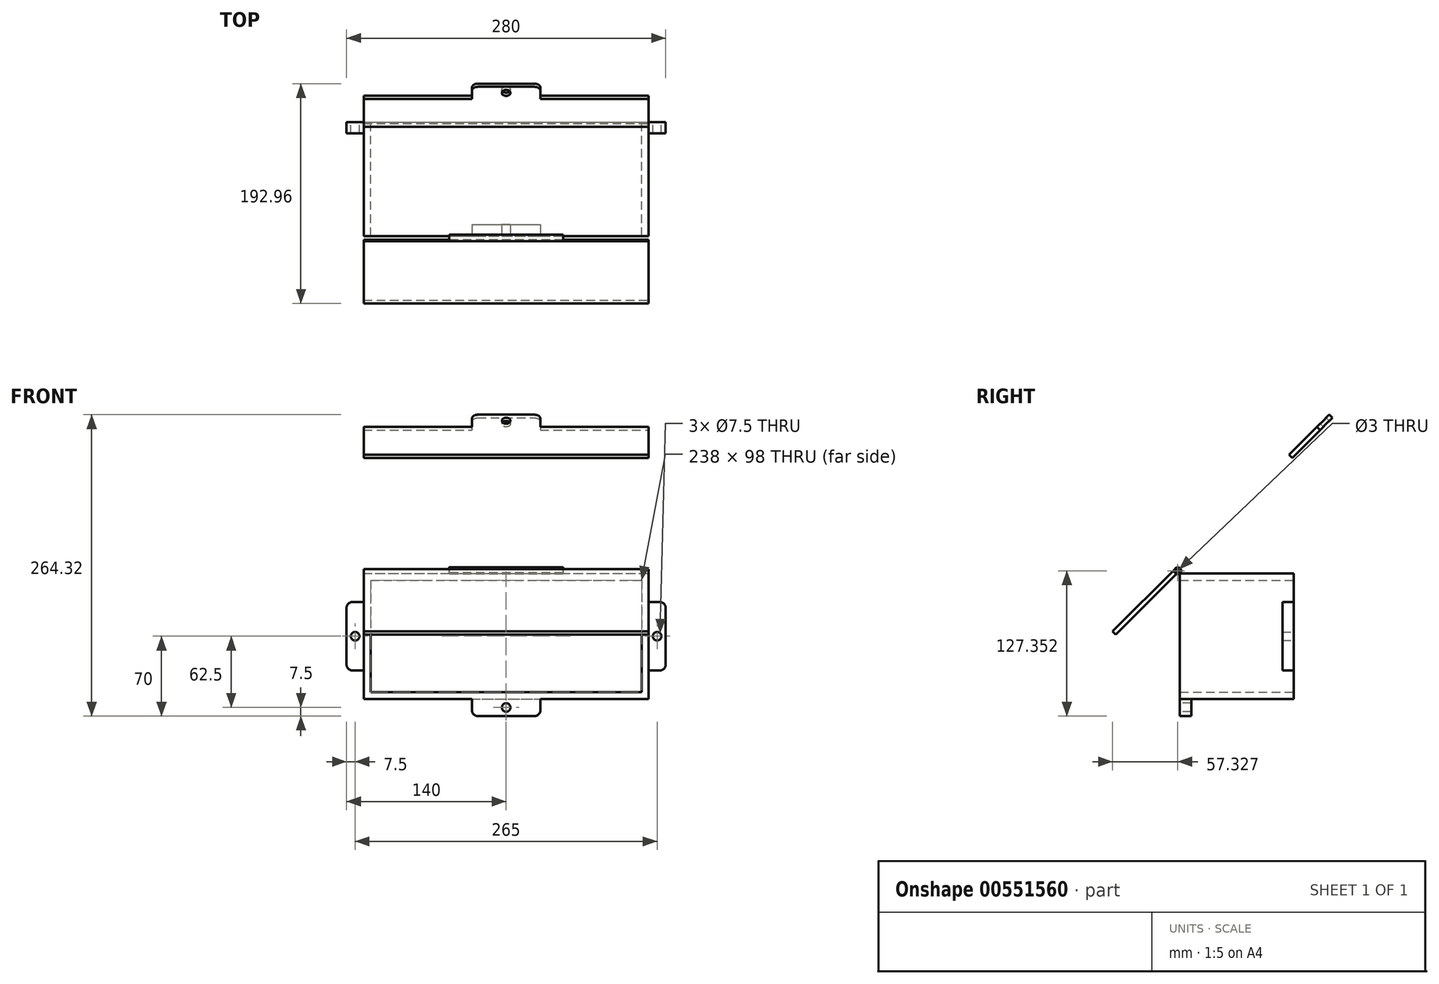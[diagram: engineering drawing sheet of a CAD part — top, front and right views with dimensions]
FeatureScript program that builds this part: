
annotation { "Feature Type Name" : "Feature", "Feature Type Description" : "" }
export const myFeature = defineFeature(function(context is Context, id is Id, definition is map)
    precondition{}
    {
        {
            var Q0;
            Q0=qCreatedBy(makeId("Front.planeOp"),FACE);
            var sketch = newSketch(context, id + "F0", { "sketchPlane" : qUnion([Q0])});
            skLineSegment(sketch, "E0.bottom", {"start": v(-125, 55) * mm, "end": v(125, 55) * mm});
            skLineSegment(sketch, "E0.top", {"start": v(-125, -55) * mm, "end": v(125, -55) * mm});
            skLineSegment(sketch, "E0.left", {"start": v(-125, 55) * mm, "end": v(-125, -55) * mm});
            skLineSegment(sketch, "E0.right", {"start": v(125, 55) * mm, "end": v(125, -55) * mm});
            skLineSegment(sketch, "E1", {"start": v(-125, 30) * mm, "end": v(-140, 30) * mm});
            skLineSegment(sketch, "E2", {"start": v(-140, 30) * mm, "end": v(-140, -30) * mm});
            skLineSegment(sketch, "E3", {"start": v(-140, -30) * mm, "end": v(-125, -30) * mm});
            skCircle(sketch, "E4", {"center": v(-132.5, 0) * mm, "radius": 3.75 * mm});
            skPoint(sketch, "E4.centerSnap0", {"position": v(-125, 0) * mm});
            skLineSegment(sketch, "E5", {"start": v(125, 30) * mm, "end": v(140, 30) * mm});
            skLineSegment(sketch, "E6", {"start": v(140, 30) * mm, "end": v(140, -30) * mm});
            skLineSegment(sketch, "E7", {"start": v(140, -30) * mm, "end": v(125, -30) * mm});
            skCircle(sketch, "E8", {"center": v(132.5, 0) * mm, "radius": 3.75 * mm});
            skLineSegment(sketch, "E9.bottom", {"start": v(-119, 49) * mm, "end": v(119, 49) * mm});
            skLineSegment(sketch, "E9.top", {"start": v(-119, -49) * mm, "end": v(119, -49) * mm});
            skLineSegment(sketch, "E9.left", {"start": v(-119, 49) * mm, "end": v(-119, -49) * mm});
            skLineSegment(sketch, "E9.right", {"start": v(119, 49) * mm, "end": v(119, -49) * mm});
            skSolve(sketch);
        }
        {
            var Q0;
            {var subQ4=sQuery(id+"F0.wireOp",EDGE,"E0.bottom");Q0=makeQuery(id+"F0.imprint","IMPRINT",FACE,{"disambiguationData":[TD([[makeQuery(id+"F0.imprint","IMPRINT",EDGE,{"derivedFrom":subQ4}),-1.0]])]});}
            extrude(context, id + "F1", {"entities" : qUnion([Q0]), "depth" : 100 * mm, "offsetDistance" : 25 * mm});
        }
        {
            var Q0;
            {var subQ1=sQuery(id+"F0.wireOp",EDGE,"E5");Q0=makeQuery(id+"F0.imprint","IMPRINT",FACE,{"disambiguationData":[TD([[makeQuery(id+"F0.imprint","IMPRINT",EDGE,{"derivedFrom":subQ1}),-1.0]])]});}
            var Q1;
            {var subQ1=sQuery(id+"F0.wireOp",EDGE,"E1");Q1=makeQuery(id+"F0.imprint","IMPRINT",FACE,{"disambiguationData":[TD([[makeQuery(id+"F0.imprint","IMPRINT",EDGE,{"derivedFrom":subQ1}),1.0]])]});}
            extrude(context, id + "F2", {"entities" : qUnion([Q0, Q1]), "operationType" : NewBodyOperationType.ADD, "depth" : 10 * mm, "offsetDistance" : 25 * mm});
        }
        {
            var Q0;
            Q0=makeQuery(id+"F2.opExtrude","SWEPT_EDGE",EDGE,{"disambiguationData":[OSD([sQuery(id+"F0.wireOp",EDGE,"E5"),sQuery(id+"F0.wireOp",EDGE,"E6")])]});
            var Q1;
            Q1=makeQuery(id+"F2.opExtrude","SWEPT_EDGE",EDGE,{"disambiguationData":[OSD([sQuery(id+"F0.wireOp",EDGE,"E6"),sQuery(id+"F0.wireOp",EDGE,"E7")])]});
            var Q2;
            Q2=makeQuery(id+"F2.opExtrude","SWEPT_EDGE",EDGE,{"disambiguationData":[OSD([sQuery(id+"F0.wireOp",EDGE,"E2"),sQuery(id+"F0.wireOp",EDGE,"E3")])]});
            var Q3;
            Q3=makeQuery(id+"F2.opExtrude","SWEPT_EDGE",EDGE,{"disambiguationData":[OSD([sQuery(id+"F0.wireOp",EDGE,"E1"),sQuery(id+"F0.wireOp",EDGE,"E2")])]});
            fillet(context, id + "F3", {"entities" : qUnion([Q0, Q1, Q2, Q3]), "radius" : 5 * mm, "tangentPropagation" : true, "allowEdgeOverflow" : false});
        }
        {
            var Q0;
            Q0=makeQuery(id+"F1.opExtrude","CAP_FACE",FACE,{"disambiguationData":[OSD([sQuery(id+"F0.wireOp",EDGE,"E0.bottom"),sQuery(id+"F0.wireOp",EDGE,"E0.top"),sQuery(id+"F0.wireOp",EDGE,"E0.left"),sQuery(id+"F0.wireOp",EDGE,"E0.right"),sQuery(id+"F0.wireOp",EDGE,"E9.bottom"),sQuery(id+"F0.wireOp",EDGE,"E9.top"),sQuery(id+"F0.wireOp",EDGE,"E9.left"),sQuery(id+"F0.wireOp",EDGE,"E9.right")])],"isStart":false});
            var sketch = newSketch(context, id + "F4", { "sketchPlane" : qUnion([Q0])});
            skLineSegment(sketch, "E10", {"start": v(-30, -55) * mm, "end": v(-30, -70) * mm});
            skLineSegment(sketch, "E11", {"start": v(-30, -55) * mm, "end": v(30, -55) * mm});
            skLineSegment(sketch, "E12", {"start": v(-30, -70) * mm, "end": v(30, -70) * mm});
            skLineSegment(sketch, "E13", {"start": v(30, -55) * mm, "end": v(30, -70) * mm});
            skCircle(sketch, "E14", {"center": v(0, -62.5) * mm, "radius": 3.75 * mm});
            skSolve(sketch);
        }
        {
            var Q0;
            Q0 = qSketchRegion(id + "F4", true);
            extrude(context, id + "F5", {"entities" : qUnion([Q0]), "operationType" : NewBodyOperationType.ADD, "oppositeDirection" : true, "depth" : 10 * mm, "offsetDistance" : 25 * mm});
        }
        {
            var Q0;
            Q0=makeQuery(id+"F5.opExtrude","SWEPT_EDGE",EDGE,{"disambiguationData":[OSD([sQuery(id+"F4.wireOp",EDGE,"E10"),sQuery(id+"F4.wireOp",EDGE,"E12")])]});
            var Q1;
            Q1=makeQuery(id+"F5.opExtrude","SWEPT_EDGE",EDGE,{"disambiguationData":[OSD([sQuery(id+"F4.wireOp",EDGE,"E12"),sQuery(id+"F4.wireOp",EDGE,"E13")])]});
            fillet(context, id + "F6", {"entities" : qUnion([Q0, Q1]), "radius" : 5 * mm, "tangentPropagation" : true, "allowEdgeOverflow" : false});
        }
        {
            var Q0;
            Q0=qCreatedBy(makeId("Right.planeOp"),FACE);
            var sketch = newSketch(context, id + "F7", { "sketchPlane" : qUnion([Q0])});
            skCircle(sketch, "E15", {"center": v(-101.86, 57.35) * mm, "radius": 3 * mm});
            skCircle(sketch, "E16", {"center": v(-101.86, 57.35) * mm, "radius": 1.5 * mm});
            skSolve(sketch);
        }
        {
            var Q0;
            Q0 = qSketchRegion(id + "F7", true);
            extrude(context, id + "F8", {"entities" : qUnion([Q0]), "endBound" : BoundingType.SYMMETRIC, "depth" : 100 * mm, "offsetDistance" : 25 * mm});
        }
        {
            var Q0;
            {var subQ1=sQuery(id+"F0.wireOp",EDGE,"E0.left");var subQ2=sQuery(id+"F0.wireOp",EDGE,"E0.top");Q0=makeQuery(id+"F5.boolean.opBoolean","SPLIT",EDGE,{"disambiguationData":[TD([makeQuery(id+"F1.opExtrude","SWEPT_FACE",FACE,{"disambiguationData":[OSD([subQ1])]})])],"derivedFrom":makeQuery(id+"F1.opExtrude","CAP_EDGE",EDGE,{"disambiguationData":[OSD([subQ2])],"isStart":false})});}
            cPlane(context, id + "F9", {"entities" : qUnion([Q0]), "cplaneType" : CPlaneType.LINE_ANGLE, "offset" : 25 * mm, "angle" : 45 * degree, "width" : 150 * mm, "height" : 150 * mm});
        }
        {
            var Q0;
            Q0=qCreatedBy(id+"F9.planeOp",FACE);
            var sketch = newSketch(context, id + "F10", { "sketchPlane" : qUnion([Q0])});
            skLineSegment(sketch, "E17.bottom", {"start": v(125, 115.53) * mm, "end": v(-125, 115.53) * mm});
            skLineSegment(sketch, "E17.top", {"start": v(125, 111.53) * mm, "end": v(-125, 111.53) * mm});
            skLineSegment(sketch, "E17.left", {"start": v(125, 115.53) * mm, "end": v(125, 111.53) * mm});
            skLineSegment(sketch, "E17.right", {"start": v(-125, 115.53) * mm, "end": v(-125, 111.53) * mm});
            skSolve(sketch);
        }
        {
            var Q0;
            Q0 = qSketchRegion(id + "F10", true);
            var Q1;
            Q1=makeQuery(id+"F8.opExtrude","SWEPT_FACE",FACE,{"disambiguationData":[OSD([sQuery(id+"F7.wireOp",EDGE,"E15")])]});
            extrude(context, id + "F11", {"entities" : qUnion([Q0]), "operationType" : NewBodyOperationType.ADD, "endBound" : BoundingType.UP_TO_SURFACE, "depth" : 25 * mm, "endBoundEntityFace" : qUnion([Q1]), "offsetDistance" : 25 * mm});
        }
        {
            var Q0;
            Q0=makeQuery(id+"F11.opExtrude","SWEPT_FACE",FACE,{"disambiguationData":[OSD([sQuery(id+"F10.wireOp",EDGE,"E17.top")])]});
            var sketch = newSketch(context, id + "F12", { "sketchPlane" : qUnion([Q0])});
            skLineSegment(sketch, "E18", {"start": v(87.5, 34.28) * mm, "end": v(-125, 34.28) * mm});
            skLineSegment(sketch, "E19", {"start": v(125, 109.6) * mm, "end": v(-125, 109.6) * mm});
            skLineSegment(sketch, "E20", {"start": v(125, 109.6) * mm, "end": v(125, 144.28) * mm});
            skLineSegment(sketch, "E21", {"start": v(125, 144.28) * mm, "end": v(30, 144.28) * mm});
            skLineSegment(sketch, "E22", {"start": v(-125, 144.28) * mm, "end": v(-125, 109.6) * mm});
            skLineSegment(sketch, "E23", {"start": v(30, 144.28) * mm, "end": v(30, 159.28) * mm});
            skLineSegment(sketch, "E24", {"start": v(30, 159.28) * mm, "end": v(-30, 159.28) * mm});
            skLineSegment(sketch, "E25", {"start": v(-30, 159.28) * mm, "end": v(-30, 144.28) * mm});
            skLineSegment(sketch, "E26.trimOffspring", {"start": v(-30, 144.28) * mm, "end": v(-125, 144.28) * mm});
            skCircle(sketch, "E27", {"center": v(0, 151.78) * mm, "radius": 3.75 * mm});
            skSolve(sketch);
        }
        {
            var Q0;
            Q0 = qSketchRegion(id + "F12", true);
            extrude(context, id + "F13", {"entities" : qUnion([Q0]), "operationType" : NewBodyOperationType.ADD, "oppositeDirection" : true, "depth" : 4 * mm, "offsetDistance" : 25 * mm});
        }
        {
            var Q0;
            Q0=makeQuery(id+"F13.opExtrude","SWEPT_EDGE",EDGE,{"disambiguationData":[OSD([sQuery(id+"F12.wireOp",EDGE,"E23"),sQuery(id+"F12.wireOp",EDGE,"E24")])]});
            var Q1;
            Q1=makeQuery(id+"F13.opExtrude","SWEPT_EDGE",EDGE,{"disambiguationData":[OSD([sQuery(id+"F12.wireOp",EDGE,"E24"),sQuery(id+"F12.wireOp",EDGE,"E25")])]});
            fillet(context, id + "F14", {"entities" : qUnion([Q0, Q1]), "radius" : 5 * mm, "tangentPropagation" : true, "allowEdgeOverflow" : false});
        }
        {
            var Q0;
            Q0=makeQuery(id+"F8.opExtrude","SWEPT_BODY",BODY,{"disambiguationData":[OSD([sQuery(id+"F7.wireOp",EDGE,"E15"),sQuery(id+"F7.wireOp",EDGE,"E16")])]});
            var Q1;
            Q1=makeQuery(id+"F8.opExtrude","CAP_EDGE",EDGE,{"disambiguationData":[OSD([sQuery(id+"F7.wireOp",EDGE,"E16")])],"isStart":false});
            transform(context, id + "F15", {"entities" : qUnion([Q0]), "transformType" : TransformType.ROTATION, "transformAxis" : qUnion([Q1]), "angle" : 0 * degree, "makeCopy" : false});
        }
    });
